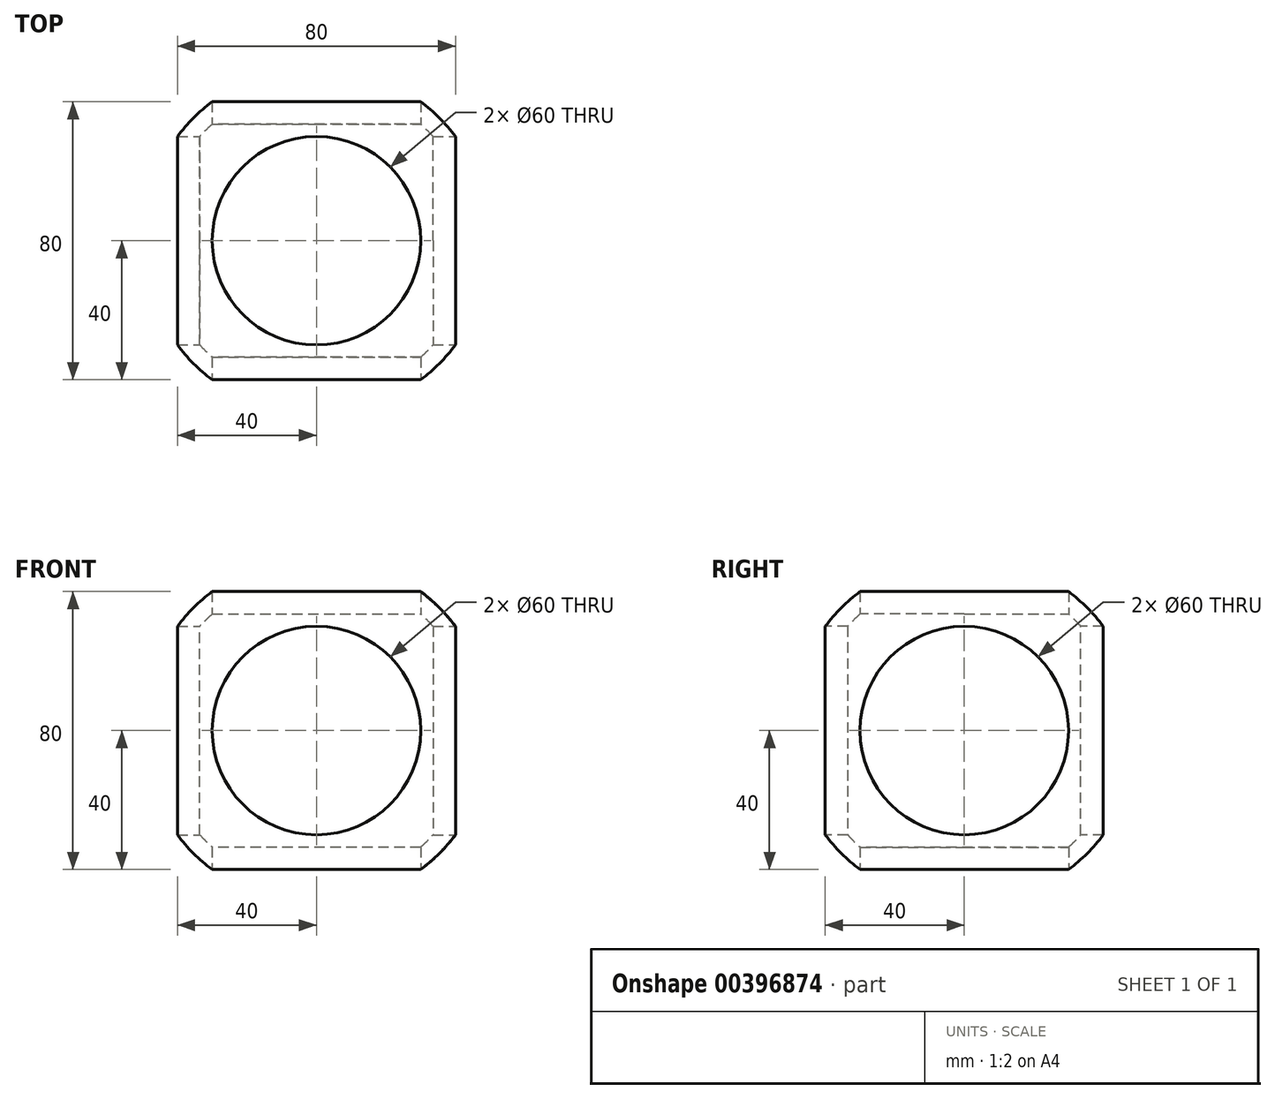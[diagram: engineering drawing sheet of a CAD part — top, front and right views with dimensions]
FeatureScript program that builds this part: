
annotation { "Feature Type Name" : "Feature", "Feature Type Description" : "" }
export const myFeature = defineFeature(function(context is Context, id is Id, definition is map)
    precondition{}
    {
        {
            var Q0;
            Q0=qCreatedBy(makeId("Front.planeOp"),FACE);
            var sketch = newSketch(context, id + "F0", { "sketchPlane" : qUnion([Q0])});
            skLineSegment(sketch, "E0", {"start": v(0, 0) * mm, "end": v(0, 50) * mm});
            skLineSegment(sketch, "E1", {"start": v(0, 0) * mm, "end": v(0, -50) * mm});
            skArc(sketch, "E2", {"start": v(0, 50) * mm, "mid": v(-50, 0) * mm, "end": v(0, -50) * mm});
            skSolve(sketch);
        }
        {
            var Q0;
            Q0=makeQuery(id+"F0.imprint","IMPRINT",FACE,{"disambiguationData":[TD([[makeQuery(id+"F0.imprint","IMPRINT",EDGE,{"derivedFrom":sQuery(id+"F0.wireOp",EDGE,"E0")}),1.0]])]});
            var Q1;
            Q1=sQuery(id+"F0.wireOp",EDGE,"E0");
            revolve(context, id + "F1", {"entities" : qUnion([Q0]), "axis" : qUnion([Q1]), "revolveType" : RevolveType.FULL});
        }
        {
            var Q0;
            Q0=qCreatedBy(makeId("Front.planeOp"),FACE);
            var sketch = newSketch(context, id + "F2", { "sketchPlane" : qUnion([Q0])});
            skCircle(sketch, "E3", {"center": v(0, 0) * mm, "radius": 30 * mm});
            skSolve(sketch);
        }
        {
            var Q0;
            Q0 = qSketchRegion(id + "F2", true);
            extrude(context, id + "F3", {"entities" : qUnion([Q0]), "operationType" : NewBodyOperationType.REMOVE, "endBound" : BoundingType.THROUGH_ALL, "oppositeDirection" : true, "depth" : 25 * mm, "hasSecondDirection" : true, "secondDirectionBound" : SecondDirectionBoundingType.THROUGH_ALL, "secondDirectionOppositeDirection" : false, "secondDirectionDepth" : 25 * mm});
        }
        {
            var Q0;
            Q0=qCreatedBy(makeId("Right.planeOp"),FACE);
            var sketch = newSketch(context, id + "F4", { "sketchPlane" : qUnion([Q0])});
            skCircle(sketch, "E4", {"center": v(0, 0) * mm, "radius": 30 * mm});
            skSolve(sketch);
        }
        {
            var Q0;
            Q0 = qSketchRegion(id + "F4", true);
            extrude(context, id + "F5", {"entities" : qUnion([Q0]), "operationType" : NewBodyOperationType.REMOVE, "endBound" : BoundingType.THROUGH_ALL, "oppositeDirection" : true, "depth" : 25 * mm, "hasSecondDirection" : true, "secondDirectionBound" : SecondDirectionBoundingType.THROUGH_ALL, "secondDirectionOppositeDirection" : false, "secondDirectionDepth" : 25 * mm});
        }
        {
            var Q0;
            Q0=qCreatedBy(makeId("Top.planeOp"),FACE);
            var sketch = newSketch(context, id + "F6", { "sketchPlane" : qUnion([Q0])});
            skCircle(sketch, "E5", {"center": v(0, 0) * mm, "radius": 30 * mm});
            skSolve(sketch);
        }
        {
            var Q0;
            Q0=makeQuery(id+"F6.imprint","IMPRINT",FACE,{"disambiguationData":[TD([[makeQuery(id+"F6.imprint","IMPRINT",EDGE,{"derivedFrom":sQuery(id+"F6.wireOp",EDGE,"E5")}),1.0]])]});
            var Q1;
            Q1=sQuery(id+"F6.wireOp",EDGE,"E5");
            extrude(context, id + "F7", {"entities" : qUnion([Q0]), "operationType" : NewBodyOperationType.REMOVE, "surfaceEntities" : qUnion([Q1]), "endBound" : BoundingType.THROUGH_ALL, "depth" : 25 * mm, "hasSecondDirection" : true, "secondDirectionBound" : SecondDirectionBoundingType.THROUGH_ALL, "secondDirectionOppositeDirection" : true, "secondDirectionDepth" : 25 * mm});
        }
        {
            var Q0;
            Q0=qCreatedBy(makeId("Front.planeOp"),FACE);
            var sketch = newSketch(context, id + "F8", { "sketchPlane" : qUnion([Q0])});
            skLineSegment(sketch, "E6", {"start": v(0, 0) * mm, "end": v(0, 45) * mm});
            skLineSegment(sketch, "E7", {"start": v(0, 0) * mm, "end": v(0, -45) * mm});
            skArc(sketch, "E8", {"start": v(0, 45) * mm, "mid": v(-45, 0) * mm, "end": v(0, -45) * mm});
            skSolve(sketch);
        }
        {
            var Q0;
            Q0 = qSketchRegion(id + "FgK7H3MlUTTxI94_1", true);
            var Q1;
            Q1=makeQuery(id+"F8.imprint","IMPRINT",FACE,{"disambiguationData":[TD([[makeQuery(id+"F8.imprint","IMPRINT",EDGE,{"derivedFrom":sQuery(id+"F8.wireOp",EDGE,"E6")}),1.0]])]});
            var Q2;
            Q2=sQuery(id+"F8.wireOp",EDGE,"E6");
            revolve(context, id + "F9", {"operationType" : NewBodyOperationType.REMOVE, "entities" : qUnion([Q0, Q1]), "axis" : qUnion([Q2]), "revolveType" : RevolveType.FULL, "oppositeDirection" : true});
        }
    });
